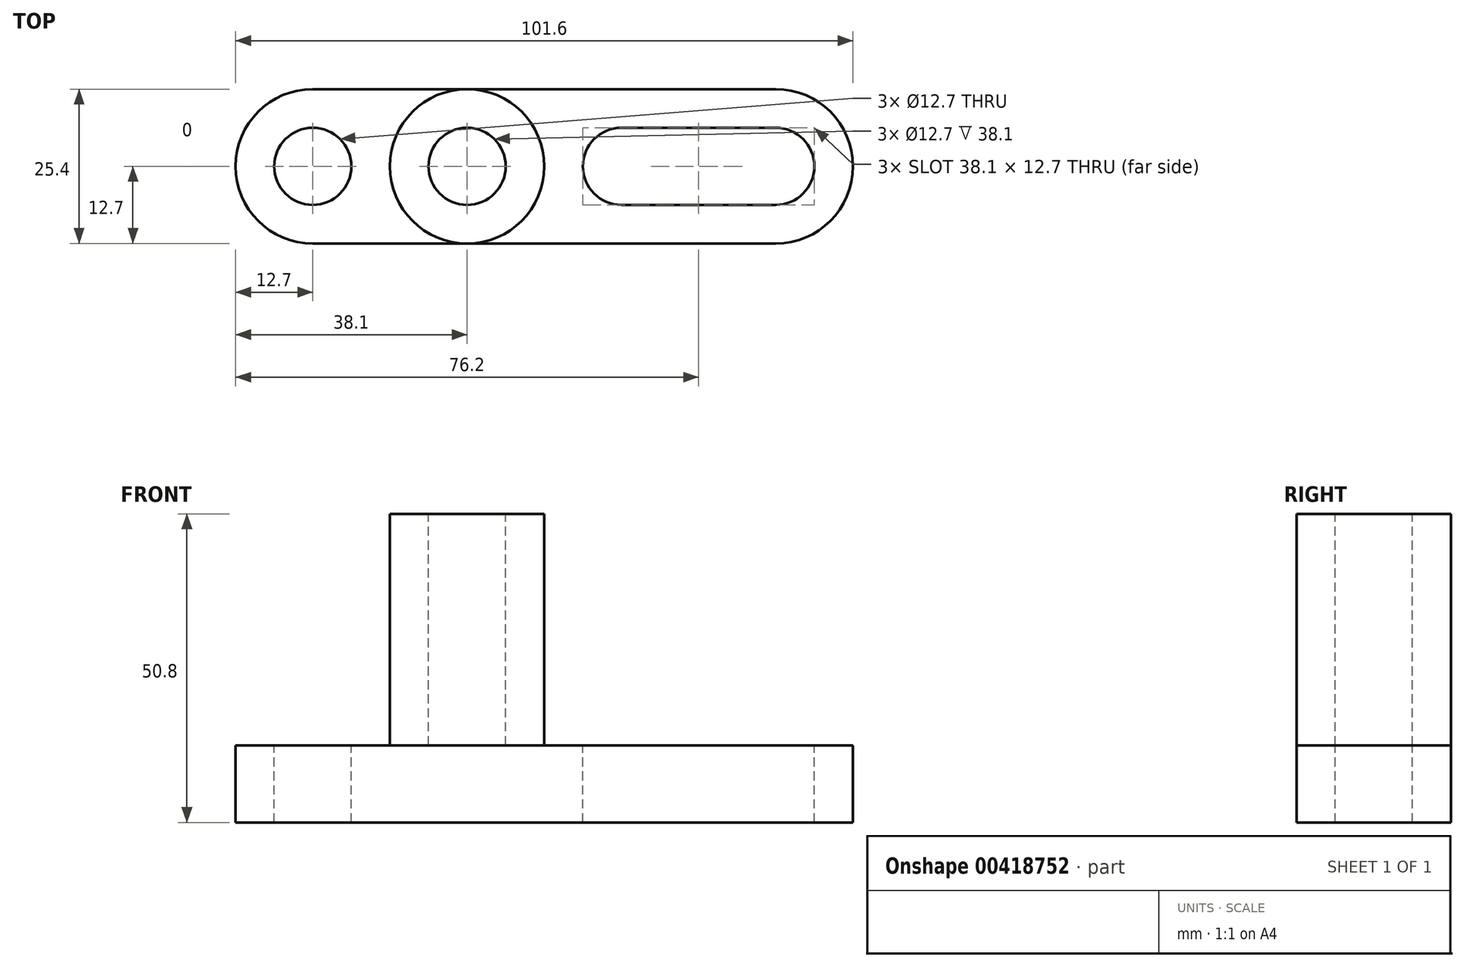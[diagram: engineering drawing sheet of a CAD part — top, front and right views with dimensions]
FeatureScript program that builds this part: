
annotation { "Feature Type Name" : "Feature", "Feature Type Description" : "" }
export const myFeature = defineFeature(function(context is Context, id is Id, definition is map)
    precondition{}
    {
        {
            var Q0;
            Q0=qCreatedBy(makeId("Front.planeOp"),FACE);
            var sketch = newSketch(context, id + "F0", { "sketchPlane" : qUnion([Q0])});
            skLineSegment(sketch, "E0", {"start": v(0, 0) * mm, "end": v(101.6, 0) * mm});
            skLineSegment(sketch, "E1", {"start": v(101.6, 0) * mm, "end": v(101.6, 12.7) * mm});
            skLineSegment(sketch, "E2", {"start": v(101.6, 12.7) * mm, "end": v(50.8, 12.7) * mm});
            skLineSegment(sketch, "E3", {"start": v(50.8, 12.7) * mm, "end": v(50.8, 50.8) * mm});
            skLineSegment(sketch, "E4", {"start": v(50.8, 50.8) * mm, "end": v(25.4, 50.8) * mm});
            skLineSegment(sketch, "E5", {"start": v(25.4, 50.8) * mm, "end": v(25.4, 12.7) * mm});
            skLineSegment(sketch, "E6", {"start": v(25.4, 12.7) * mm, "end": v(0, 12.7) * mm});
            skLineSegment(sketch, "E7", {"start": v(0, 12.7) * mm, "end": v(0, 0) * mm});
            skSolve(sketch);
        }
        {
            var Q0;
            Q0=makeQuery(id+"F0.imprint","IMPRINT",FACE,{"disambiguationData":[TD([[makeQuery(id+"F0.imprint","IMPRINT",EDGE,{"derivedFrom":sQuery(id+"F0.wireOp",EDGE,"E0")}),1.0]])]});
            extrude(context, id + "F1", {"entities" : qUnion([Q0]), "depth" : 25.4 * mm});
        }
        {
            var Q0;
            Q0=makeQuery(id+"F1.opExtrude","SWEPT_FACE",FACE,{"disambiguationData":[OSD([sQuery(id+"F0.wireOp",EDGE,"E6")])]});
            var sketch = newSketch(context, id + "F2", { "sketchPlane" : qUnion([Q0])});
            skCircle(sketch, "E8", {"center": v(12.7, -12.7) * mm, "radius": 6.35 * mm});
            skPoint(sketch, "E8.centerSnap0", {"position": v(12.7, 0) * mm});
            skArc(sketch, "E9", {"start": v(12.7, 0) * mm, "mid": v(0, -12.7) * mm, "end": v(12.7, -25.4) * mm});
            skSolve(sketch);
        }
        {
            var Q0;
            Q0=makeQuery(id+"F2.imprint","IMPRINT",FACE,{"disambiguationData":[TD([[makeQuery(id+"F2.imprint","IMPRINT",EDGE,{"derivedFrom":sQuery(id+"F2.wireOp",EDGE,"E8")}),1.0]])]});
            var Q1;
            {var subQ0=sQuery(id+"F2.wireOp",EDGE,"E9");var subQ1=sQuery(id+"F0.wireOp",EDGE,"E6");var subQ2=makeQuery(id+"F1.opExtrude","CAP_EDGE",EDGE,{"disambiguationData":[OSD([subQ1])],"isStart":true});var subQ3=makeQuery(id+"F2.imprint","INTERSECT",VERTEX,{"derivedFrom":[subQ2,subQ0]});Q1=makeQuery(id+"F2.imprint","IMPRINT",FACE,{"disambiguationData":[TD([[makeQuery(id+"F2.imprint","IMPRINT",EDGE,{"disambiguationData":[TD([[subQ3,-1.0]])],"derivedFrom":subQ0}),-1.0]])]});}
            var Q2;
            {var subQ0=sQuery(id+"F2.wireOp",EDGE,"E9");var subQ1=sQuery(id+"F0.wireOp",EDGE,"E6");var subQ2=makeQuery(id+"F1.opExtrude","CAP_EDGE",EDGE,{"disambiguationData":[OSD([subQ1])],"isStart":false});var subQ3=makeQuery(id+"F2.imprint","INTERSECT",VERTEX,{"derivedFrom":[subQ2,subQ0]});Q2=makeQuery(id+"F2.imprint","IMPRINT",FACE,{"disambiguationData":[TD([[makeQuery(id+"F2.imprint","IMPRINT",EDGE,{"disambiguationData":[TD([[subQ3,1.0]])],"derivedFrom":subQ0}),-1.0]])]});}
            extrude(context, id + "F3", {"entities" : qUnion([Q0, Q1, Q2]), "operationType" : NewBodyOperationType.REMOVE, "oppositeDirection" : true, "depth" : 25.4 * mm});
        }
        {
            var Q0;
            Q0=makeQuery(id+"F1.opExtrude","SWEPT_FACE",FACE,{"disambiguationData":[OSD([sQuery(id+"F0.wireOp",EDGE,"E4")])]});
            var sketch = newSketch(context, id + "F4", { "sketchPlane" : qUnion([Q0])});
            skCircle(sketch, "E10", {"center": v(38.1, -12.7) * mm, "radius": 6.35 * mm});
            skPoint(sketch, "E10.centerSnap0", {"position": v(38.1, 0) * mm});
            skCircle(sketch, "E11", {"center": v(38.1, -12.7) * mm, "radius": 12.7 * mm});
            skSolve(sketch);
        }
        {
            var Q0;
            {var subQ0=sQuery(id+"F4.wireOp",EDGE,"E11");var subQ1=sQuery(id+"F0.wireOp",EDGE,"E4");var subQ2=makeQuery(id+"F1.opExtrude","CAP_EDGE",EDGE,{"disambiguationData":[OSD([subQ1])],"isStart":true});var subQ3=makeQuery(id+"F4.imprint","INTERSECT",VERTEX,{"derivedFrom":[subQ2,subQ0]});Q0=makeQuery(id+"F4.imprint","IMPRINT",FACE,{"disambiguationData":[TD([[makeQuery(id+"F4.imprint","IMPRINT",EDGE,{"disambiguationData":[TD([[subQ3,-1.0]])],"derivedFrom":subQ0}),-1.0]])]});}
            var Q1;
            Q1=makeQuery(id+"F4.imprint","IMPRINT",FACE,{"disambiguationData":[TD([[makeQuery(id+"F4.imprint","IMPRINT",EDGE,{"derivedFrom":sQuery(id+"F4.wireOp",EDGE,"E10")}),1.0]])]});
            var Q2;
            {var subQ0=sQuery(id+"F4.wireOp",EDGE,"E11");var subQ1=sQuery(id+"F0.wireOp",EDGE,"E4");var subQ2=makeQuery(id+"F1.opExtrude","CAP_EDGE",EDGE,{"disambiguationData":[OSD([subQ1])],"isStart":true});var subQ3=makeQuery(id+"F4.imprint","INTERSECT",VERTEX,{"derivedFrom":[subQ2,subQ0]});Q2=makeQuery(id+"F4.imprint","IMPRINT",FACE,{"disambiguationData":[TD([[makeQuery(id+"F4.imprint","IMPRINT",EDGE,{"disambiguationData":[TD([[subQ3,1.0]])],"derivedFrom":subQ0}),-1.0]])]});}
            var Q3;
            {var subQ0=sQuery(id+"F4.wireOp",EDGE,"E11");var subQ1=sQuery(id+"F0.wireOp",EDGE,"E4");var subQ4=makeQuery(id+"F1.opExtrude","CAP_EDGE",EDGE,{"disambiguationData":[OSD([subQ1])],"isStart":false});var subQ5=makeQuery(id+"F4.imprint","INTERSECT",VERTEX,{"derivedFrom":[subQ4,subQ0]});Q3=makeQuery(id+"F4.imprint","IMPRINT",FACE,{"disambiguationData":[TD([[makeQuery(id+"F4.imprint","IMPRINT",EDGE,{"disambiguationData":[TD([[subQ5,-1.0]])],"derivedFrom":subQ0}),-1.0]])]});}
            var Q4;
            {var subQ0=sQuery(id+"F4.wireOp",EDGE,"E11");var subQ1=sQuery(id+"F0.wireOp",EDGE,"E4");var subQ4=makeQuery(id+"F1.opExtrude","CAP_EDGE",EDGE,{"disambiguationData":[OSD([subQ1])],"isStart":false});var subQ5=makeQuery(id+"F4.imprint","INTERSECT",VERTEX,{"derivedFrom":[subQ4,subQ0]});Q4=makeQuery(id+"F4.imprint","IMPRINT",FACE,{"disambiguationData":[TD([[makeQuery(id+"F4.imprint","IMPRINT",EDGE,{"disambiguationData":[TD([[subQ5,1.0]])],"derivedFrom":subQ0}),-1.0]])]});}
            extrude(context, id + "F5", {"entities" : qUnion([Q0, Q1, Q2, Q3, Q4]), "operationType" : NewBodyOperationType.REMOVE, "oppositeDirection" : true, "depth" : 38.1 * mm});
        }
        {
            var Q0;
            {var subQ0=sQuery(id+"F0.wireOp",EDGE,"E4");var subQ1=makeQuery(id+"F1.opExtrude","CAP_EDGE",EDGE,{"disambiguationData":[OSD([subQ0])],"isStart":false});var subQ2=sQuery(id+"F0.wireOp",EDGE,"E3");var subQ3=makeQuery(id+"F1.opExtrude","SWEPT_EDGE",EDGE,{"disambiguationData":[OSD([subQ2,subQ0])]});var subQ4=makeQuery(id+"F4.imprint","INTERSECT",VERTEX,{"derivedFrom":[subQ3,subQ1]});var subQ5=sQuery(id+"F4.wireOp",EDGE,"E11");var subQ6=makeQuery(id+"F4.imprint","INTERSECT",VERTEX,{"derivedFrom":[subQ1,subQ5]});var subQ8=makeQuery(id+"F1.opExtrude","CAP_EDGE",EDGE,{"disambiguationData":[OSD([subQ0])],"isStart":true});var subQ9=makeQuery(id+"F4.imprint","INTERSECT",VERTEX,{"derivedFrom":[subQ3,subQ8]});var subQ10=makeQuery(id+"F4.imprint","INTERSECT",VERTEX,{"derivedFrom":[subQ8,subQ5]});Q0=makeQuery(id+"F5.boolean.opBoolean","MERGE",FACE,{"derivedFrom":[makeQuery(id+"F1.opExtrude","SWEPT_FACE",FACE,{"disambiguationData":[OSD([sQuery(id+"F0.wireOp",EDGE,"E2")])]}),makeQuery(id+"F5.opExtrude","CAP_FACE",FACE,{"disambiguationData":[OSD([subQ2,subQ0,subQ5]),TDD([makeQuery(id+"F4.imprint","IMPRINT",EDGE,{"disambiguationData":[TD([[subQ10,1.0]])],"derivedFrom":subQ5}),makeQuery(id+"F4.imprint","IMPRINT",EDGE,{"disambiguationData":[TD([[subQ9,1.0]])],"derivedFrom":subQ3}),makeQuery(id+"F4.imprint","IMPRINT",EDGE,{"disambiguationData":[TD([[subQ10,1.0]])],"derivedFrom":subQ8})])],"isStart":false}),makeQuery(id+"F5.opExtrude","CAP_FACE",FACE,{"disambiguationData":[OSD([subQ2,subQ0,subQ5]),TDD([makeQuery(id+"F4.imprint","IMPRINT",EDGE,{"disambiguationData":[TD([[subQ6,-1.0]])],"derivedFrom":subQ5}),makeQuery(id+"F4.imprint","IMPRINT",EDGE,{"disambiguationData":[TD([[subQ4,-1.0]])],"derivedFrom":subQ3}),makeQuery(id+"F4.imprint","IMPRINT",EDGE,{"disambiguationData":[TD([[subQ6,1.0]])],"derivedFrom":subQ1})])],"isStart":false})]});}
            var sketch = newSketch(context, id + "F6", { "sketchPlane" : qUnion([Q0])});
            skCircle(sketch, "E12", {"center": v(88.9, -12.7) * mm, "radius": 6.35 * mm});
            skPoint(sketch, "E12.centerSnap0", {"position": v(101.6, -12.7) * mm});
            skCircle(sketch, "E13", {"center": v(63.5, -12.7) * mm, "radius": 6.35 * mm});
            skPoint(sketch, "E13.centerSnap0", {"position": v(50.8, -12.7) * mm});
            skLineSegment(sketch, "E14", {"start": v(63.5, -6.35) * mm, "end": v(88.9, -6.35) * mm});
            skLineSegment(sketch, "E15", {"start": v(63.5, -19.05) * mm, "end": v(88.9, -19.05) * mm});
            skArc(sketch, "E16", {"start": v(88.9, -25.4) * mm, "mid": v(101.6, -12.7) * mm, "end": v(88.9, 0) * mm});
            skSolve(sketch);
        }
        {
            var Q0;
            {var subQ0=sQuery(id+"F6.wireOp",EDGE,"E14");Q0=makeQuery(id+"F6.imprint","IMPRINT",FACE,{"disambiguationData":[TD([[makeQuery(id+"F6.imprint","IMPRINT",EDGE,{"derivedFrom":subQ0}),-1.0]])]});}
            var Q1;
            {var subQ0=sQuery(id+"F6.wireOp",EDGE,"E13");var subQ1=makeQuery(id+"F6.imprint","INTERSECT",VERTEX,{"derivedFrom":[subQ0,sQuery(id+"F6.wireOp",EDGE,"E14")]});Q1=makeQuery(id+"F6.imprint","IMPRINT",FACE,{"disambiguationData":[TD([[makeQuery(id+"F6.imprint","IMPRINT",EDGE,{"disambiguationData":[TD([[subQ1,-1.0]])],"derivedFrom":subQ0}),1.0]])]});}
            var Q2;
            {var subQ0=sQuery(id+"F6.wireOp",EDGE,"E12");var subQ1=makeQuery(id+"F6.imprint","INTERSECT",VERTEX,{"derivedFrom":[subQ0,sQuery(id+"F6.wireOp",EDGE,"E14")]});Q2=makeQuery(id+"F6.imprint","IMPRINT",FACE,{"disambiguationData":[TD([[makeQuery(id+"F6.imprint","IMPRINT",EDGE,{"disambiguationData":[TD([[subQ1,-1.0]])],"derivedFrom":subQ0}),1.0]])]});}
            var Q3;
            {var subQ0=sQuery(id+"F6.wireOp",EDGE,"E16");var subQ3=sQuery(id+"F0.wireOp",EDGE,"E2");var subQ6=makeQuery(id+"F1.opExtrude","SWEPT_EDGE",EDGE,{"disambiguationData":[OSD([sQuery(id+"F0.wireOp",EDGE,"E1"),subQ3])]});var subQ7=makeQuery(id+"F6.imprint","INTERSECT",VERTEX,{"derivedFrom":[subQ6,subQ0]});Q3=makeQuery(id+"F6.imprint","IMPRINT",FACE,{"disambiguationData":[TD([[makeQuery(id+"F6.imprint","IMPRINT",EDGE,{"disambiguationData":[TD([[subQ7,-1.0]])],"derivedFrom":subQ0}),-1.0]])]});}
            var Q4;
            {var subQ0=sQuery(id+"F6.wireOp",EDGE,"E16");var subQ3=sQuery(id+"F0.wireOp",EDGE,"E2");var subQ6=makeQuery(id+"F1.opExtrude","SWEPT_EDGE",EDGE,{"disambiguationData":[OSD([sQuery(id+"F0.wireOp",EDGE,"E1"),subQ3])]});var subQ7=makeQuery(id+"F6.imprint","INTERSECT",VERTEX,{"derivedFrom":[subQ6,subQ0]});Q4=makeQuery(id+"F6.imprint","IMPRINT",FACE,{"disambiguationData":[TD([[makeQuery(id+"F6.imprint","IMPRINT",EDGE,{"disambiguationData":[TD([[subQ7,1.0]])],"derivedFrom":subQ0}),-1.0]])]});}
            extrude(context, id + "F7", {"entities" : qUnion([Q0, Q1, Q2, Q3, Q4]), "operationType" : NewBodyOperationType.REMOVE, "oppositeDirection" : true, "depth" : 25.4 * mm});
        }
    });
